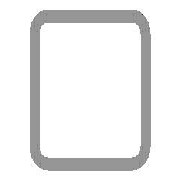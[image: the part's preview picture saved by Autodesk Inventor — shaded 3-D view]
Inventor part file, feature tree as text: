
AUTODESK INVENTOR PART (.ipt)
format: ipt  version: 2025 (Build 290162010, 162A)  size: 134,656 bytes
history: native  units: mm (DEFAULTED — no unit token found)
features: other x4, sketch x1, plane x1
ambient origin geometry x8: Origin, YZ Plane, XZ Plane, XY Plane, X Axis, Y Axis, Z Axis, Center Point
bodies: Solid1 (feature_tree), Body (feature_tree)
feature tree (6):
  parser-record x1  (decoder bookkeeping rows leaked as tree rows — omitted from the tree; the rows remain in map.json)
  other  "Driven Length"
  other  "Start Plane"
  other  "End Plane"
  sketch  "Sketch3"  dims[d3=1540.0mm d4=0.0mm d7=6.0mm d9=80.0mm d11=80.0mm d12=3.0mm d13=80.0mm d14=1620.0mm d15=40.0mm d16=40.0mm d17=90.0deg d18=1540.0mm]
  plane  "Work Plane3"
